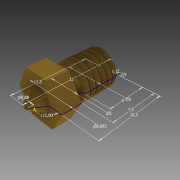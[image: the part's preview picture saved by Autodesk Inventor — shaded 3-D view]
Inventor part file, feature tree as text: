
AUTODESK INVENTOR PART (.ipt)
format: ipt  version: 2015 (Build 190159000, 159)  size: 261,120 bytes
history: native  units: mm
features: sketch x3, hole x3, other x2, chamfer x2, revolve x1, thread x1, extrude x1
ambient origin geometry x8: Origin, YZ Plane, XZ Plane, XY Plane, X Axis, Y Axis, Z Axis, Center Point
bodies: Body1 (feature_tree)
feature tree (13):
  other  "Твердое тело1"
  revolve  "Вращение1"
  chamfer  "Фаска1"  Distance=15.0mm
  thread  "Резьба1"
  sketch  "Эскиз2"
  sketch  "Эскиз3"
  hole  "Отверстие1"  [1 undecoded]
  hole  "Отверстие2"  [1 undecoded]
  chamfer  "Фаска2"  Distance=7.5mm
  hole  "Отверстие3"  [1 undecoded]
  extrude  "Выдавливание1"  Depth=5.0mm
  other  "Пружина1"
  sketch  "Эскиз4"
note: 3 required parameter values undecoded (feature->parameter linkage not recoverable at this tier; creation-order binding heuristic only, values carry confidence <= 0.55)
